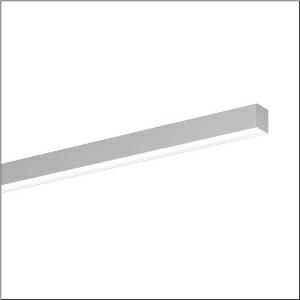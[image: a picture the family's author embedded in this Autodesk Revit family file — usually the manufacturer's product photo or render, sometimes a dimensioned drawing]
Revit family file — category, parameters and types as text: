
# Revit family: silica_r__21_51mx20da42sb_9e9a
name_source: partatom
category: Lighting Fixtures
units: mm (PartAtom-declared; Revit-internal decimal feet)

## family parameters
Cut with Voids When Loaded = No
Host = Face
Light Source = No
Part Type = Normal
Room Calculation Point = No
Round Connector Dimension = Use Diameter
Shared = No

## types (1)
- --- (1 x LED, 2400 lm, 15.2 W, 4000K)
    Apparent Load = 15 VA
    CIE Flux Codes = 48 79 96 100 100
    Color Rendering = 80
    Color Temperature = 4000K
    Default Elevation = 1800 mm
    Description = Silica® 21, office luminaire, primary optical cover: cover, of PMMA, opal, light emission: direct distribution, primary light characteristic: symmetric, installation type: surface-mounted, LED, rated luminous flux: 2.400lm, luminous efficacy: 158lm/W, light colour: 840, colour temperature: 4000K, control gear: DALI 2, with terminal, 3+2-pole, max. 2.5mm², mains connection: 220..240V, AC, 50/60Hz, rated input power: 15.2W, luminaire housing, of aluminium, metallic grey (RAL 9006), length: 1.204mm, width: 53mm, height: 53mm, protection rating (complete): IP20, insulation class (complete): insulation class I (protective earthing), certification: CE, permissible operating ambient temperature: 0..+35°C, standard: EN 50419, packaging unit: 1 piece
    Height = 53 mm
    Lamp = 1 x LED
    Lamp Light Flux = 2400 lm
    Lamp Power = 15.2 W
    Lamp count = 1
    Length = 1204 mm
    Luminous efficacy = 158 lm/W
    Manufacturer = Siteco
    ModVariant = No
    Model = 51MX20DA42SB
    Mounting Place = Ceiling
    Mounting Type = Surface mounted
    Number of Poles = 1
    OnlyDefault = Yes
    Power Factor = 1
    Product Name = Silica® 21
    Product group = office luminaire | ceiling mounted
    ProductGroupID = 303
    Protection Class = Protection class I
    Protection Degree = IP 20
    RLX_Detail_Level = 1
    RLX_Emergency_Light_Flux = 0 lm
    RLX_Emergency_Type = 0
    RLX_Emergency_Type_DB = No
    RlxData = <blob elided: 26305 chars, md5=d51b12ad>
    Socket = socket
    Standby Power = 0 W
    System Light Flux = 2400 lm
    System Power = 15 W
    Type Comments = factory setting: luminous flux: 100 % | dim-lin: 254 | 218 mA
    Type Image = l_1335933.jpg
    URL = http://relux.com
    VarID = @adj_026667
    Voltage = 0 V
    Weight = 0.00 kg
    Width = 53 mm

## geometry (parser evidence)
native form markers: Blend x4, Sweep x13
no freeform markers — native parametric forms only
